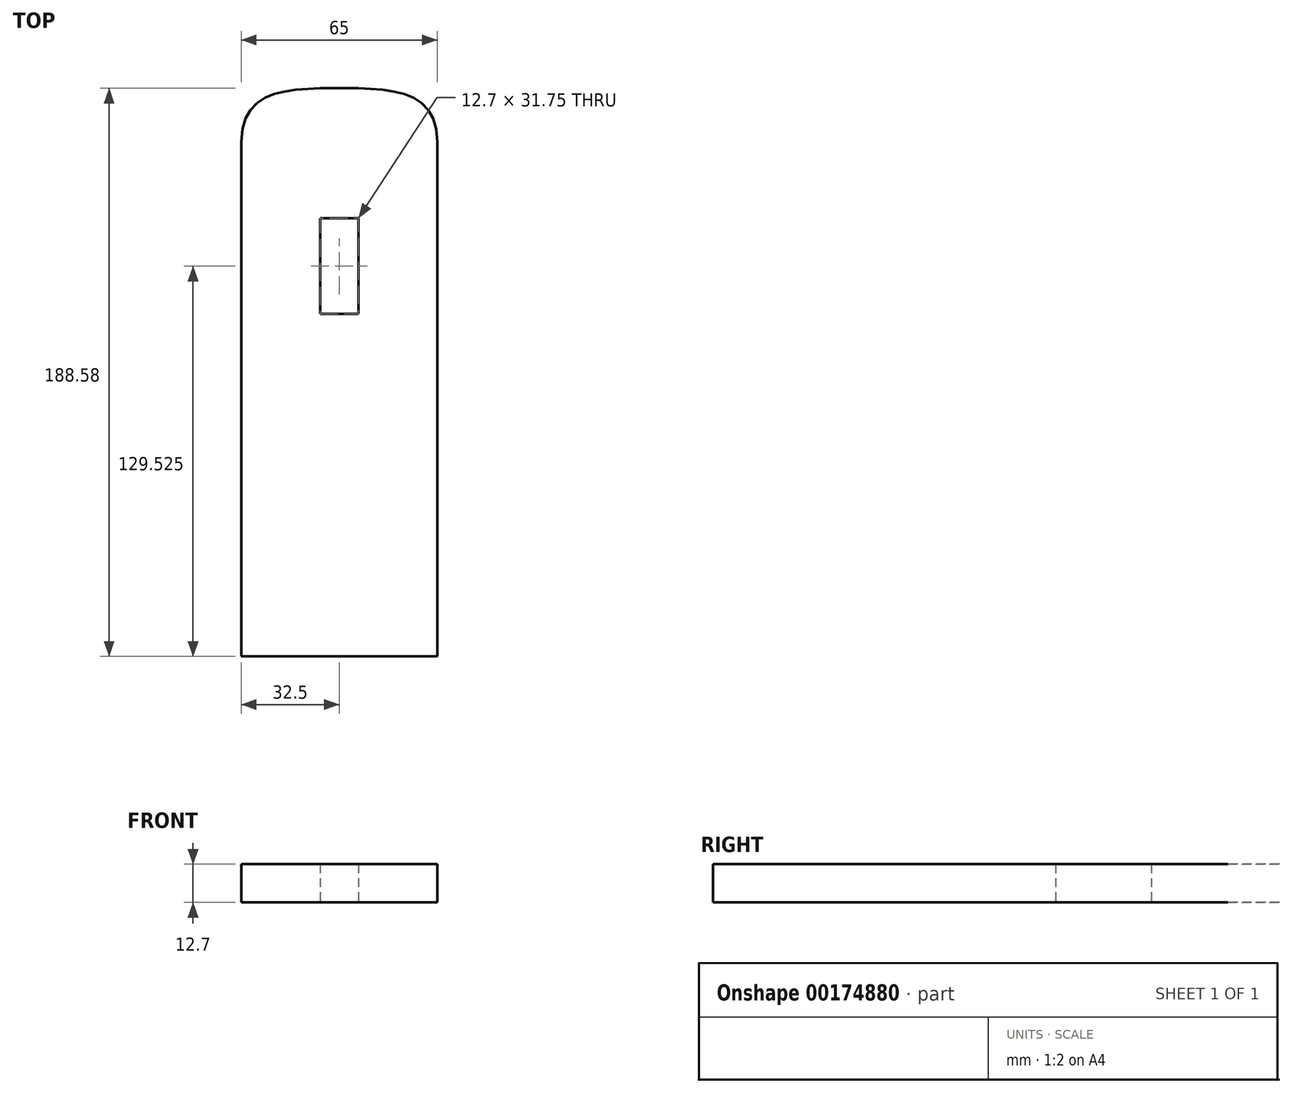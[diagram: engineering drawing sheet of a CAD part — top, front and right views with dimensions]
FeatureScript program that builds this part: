
annotation { "Feature Type Name" : "Feature", "Feature Type Description" : "" }
export const myFeature = defineFeature(function(context is Context, id is Id, definition is map)
    precondition{}
    {
        {
            var Q0;
            Q0=qCreatedBy(makeId("Top.planeOp"),FACE);
            var sketch = newSketch(context, id + "F0", { "sketchPlane" : qUnion([Q0])});
            skLineSegment(sketch, "E0.bottom", {"start": v(-32.5, -60) * mm, "end": v(32.5, -60) * mm});
            skLineSegment(sketch, "E0.top", {"start": v(-32.5, 60) * mm, "end": v(32.5, 60) * mm, "construction": true});
            skLineSegment(sketch, "E0.left", {"start": v(-32.5, -60) * mm, "end": v(-32.5, 60) * mm});
            skLineSegment(sketch, "E0.right", {"start": v(32.5, -60) * mm, "end": v(32.5, 60) * mm});
            skPoint(sketch, "E0.middle", {"position": v(0, 0) * mm});
            skLineSegment(sketch, "E1", {"start": v(-32.5, 60) * mm, "end": v(-32.5, 110.8) * mm});
            skLineSegment(sketch, "E2", {"start": v(0, 0) * mm, "end": v(0, 110.8) * mm, "construction": true});
            skLineSegment(sketch, "E3.MirrorCS", {"start": v(32.5, 60) * mm, "end": v(32.5, 110.8) * mm});
            skFitSpline(sketch, "E4", {"points": [v(-32.5, 110.8) * mm, v(0, 128.58) * mm, v(32.5, 110.8) * mm], "startDerivative": vector(0, 106.68) * mm, "endDerivative": vector(0, -106.68) * mm});
            skLineSegment(sketch, "E5.bottom", {"start": v(6.35, 53.65) * mm, "end": v(-6.35, 53.65) * mm});
            skLineSegment(sketch, "E5.top", {"start": v(6.35, 85.4) * mm, "end": v(-6.35, 85.4) * mm});
            skLineSegment(sketch, "E5.left", {"start": v(6.35, 53.65) * mm, "end": v(6.35, 85.4) * mm});
            skLineSegment(sketch, "E5.right", {"start": v(-6.35, 53.65) * mm, "end": v(-6.35, 85.4) * mm});
            skPoint(sketch, "E5.middle", {"position": v(0, 69.53) * mm});
            skSolve(sketch);
        }
        {
            var Q0;
            Q0=makeQuery(id+"F0.imprint","IMPRINT",FACE,{"disambiguationData":[TD([[makeQuery(id+"F0.imprint","IMPRINT",EDGE,{"derivedFrom":sQuery(id+"F0.wireOp",EDGE,"E0.bottom")}),1.0]])]});
            extrude(context, id + "F1", {"entities" : qUnion([Q0]), "depth" : 12.7 * mm});
        }
    });
